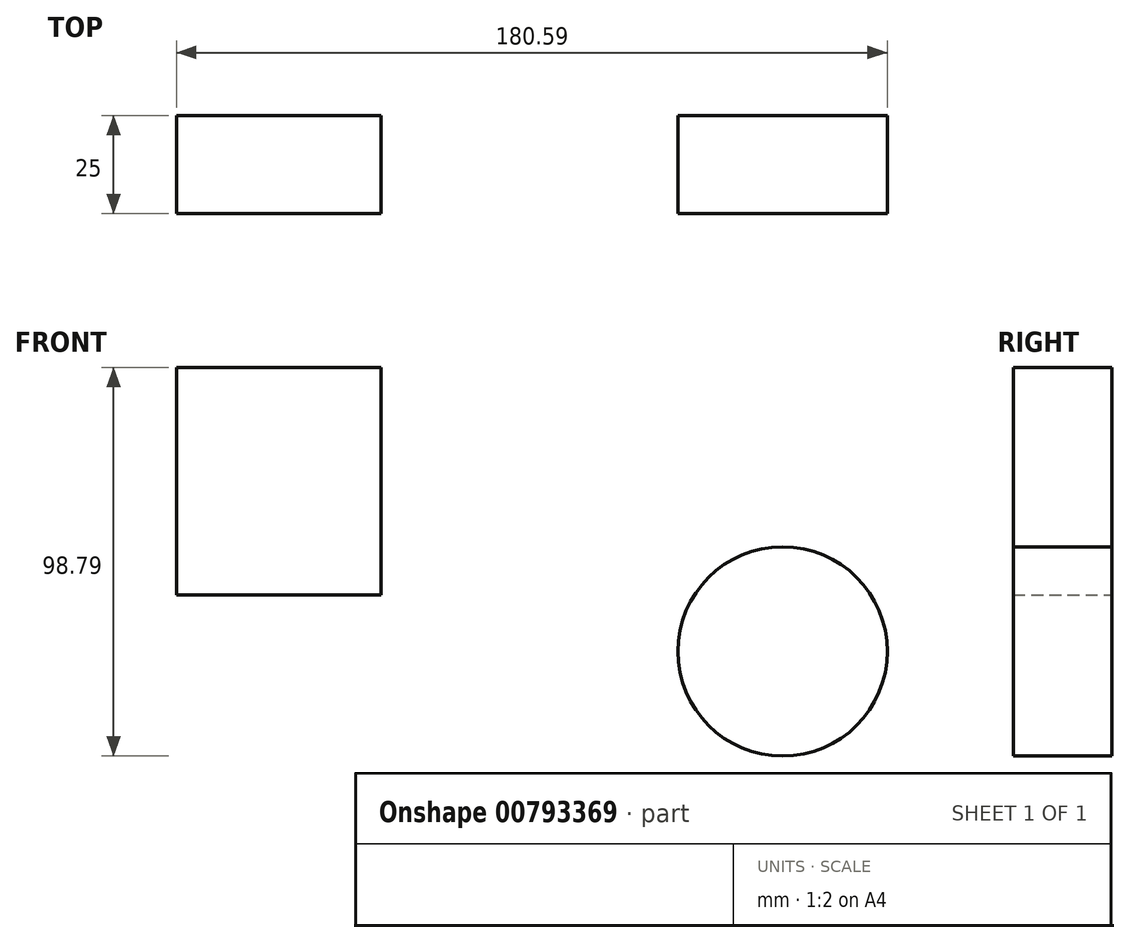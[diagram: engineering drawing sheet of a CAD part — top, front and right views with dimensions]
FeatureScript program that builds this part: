
annotation { "Feature Type Name" : "Feature", "Feature Type Description" : "" }
export const myFeature = defineFeature(function(context is Context, id is Id, definition is map)
    precondition{}
    {
        {
            var Q0;
            Q0=qCreatedBy(makeId("Front.planeOp"),FACE);
            var sketch = newSketch(context, id + "F0", { "sketchPlane" : qUnion([Q0])});
            skLineSegment(sketch, "E0.bottom", {"start": v(-82.7, 42.3) * mm, "end": v(-30.74, 42.3) * mm});
            skLineSegment(sketch, "E0.top", {"start": v(-82.7, -15.61) * mm, "end": v(-30.74, -15.61) * mm});
            skLineSegment(sketch, "E0.left", {"start": v(-82.7, 42.3) * mm, "end": v(-82.7, -15.61) * mm});
            skLineSegment(sketch, "E0.right", {"start": v(-30.74, 42.3) * mm, "end": v(-30.74, -15.61) * mm});
            skCircle(sketch, "E1", {"center": v(71.28, -29.9) * mm, "radius": 26.6 * mm});
            skSolve(sketch);
        }
        {
            var Q0;
            Q0 = qSketchRegion(id + "F0", true);
            extrude(context, id + "F1", {"entities" : qUnion([Q0]), "depth" : 25 * mm, "offsetDistance" : 25 * mm});
        }
    });
